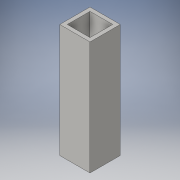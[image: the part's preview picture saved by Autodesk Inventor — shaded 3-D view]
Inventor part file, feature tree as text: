
AUTODESK INVENTOR PART (.ipt)
format: ipt  version: 2016 (Build 200138000, 138)  size: 94,720 bytes
history: native  units: in
note: dims shown in document units (in); Inventor stores cm internally (conversion verified against a paired STEP export)
features: extrude x1, sketch x1
ambient origin geometry x8: Origin, YZ Plane, XZ Plane, XY Plane, X Axis, Y Axis, Z Axis, Center Point
bodies: Solid1 (feature_tree)
feature tree (2):
  extrude  "Extrusion1"  Depth=1.0in
  sketch  "Sketch1"  dims[d0=1.0in d1=1.0in d2=0.125in d3=0.125in d4=0.125in d5=0.125in d6=3.75in d7=0.0in]
